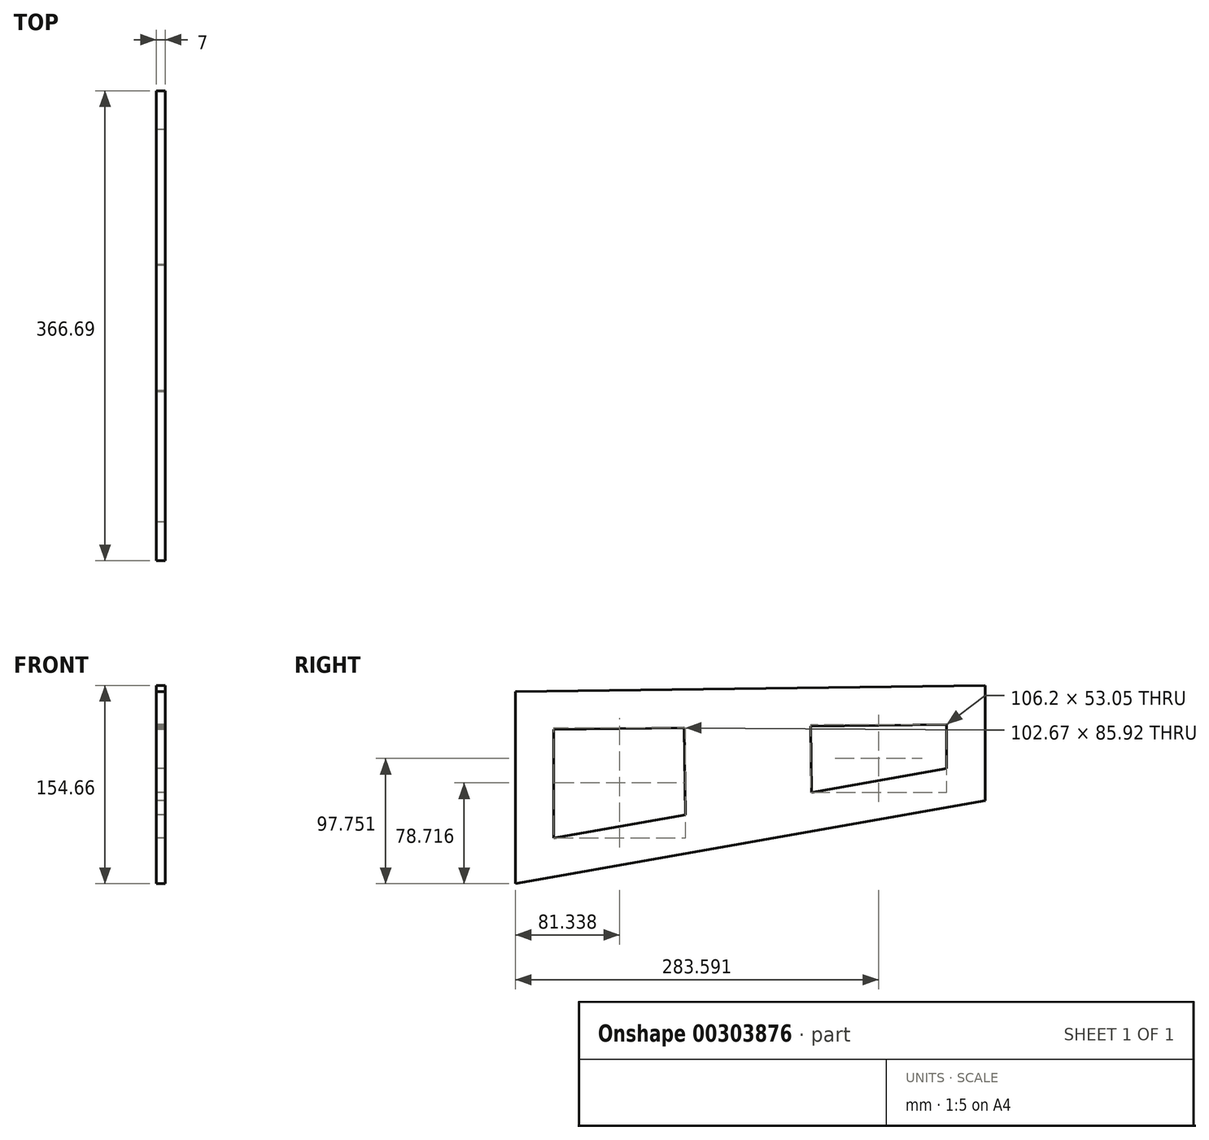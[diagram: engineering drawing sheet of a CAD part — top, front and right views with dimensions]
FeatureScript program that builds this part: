
annotation { "Feature Type Name" : "Feature", "Feature Type Description" : "" }
export const myFeature = defineFeature(function(context is Context, id is Id, definition is map)
    precondition{}
    {
        {
            var Q0;
            Q0=qCreatedBy(makeId("Right.planeOp"),FACE);
            var sketch = newSketch(context, id + "F0", { "sketchPlane" : qUnion([Q0])});
            skLineSegment(sketch, "E0.left", {"start": v(232.42, 105.9) * mm, "end": v(232.42, -44.1) * mm});
            skLineSegment(sketch, "E1.bottom", {"start": v(232.42, 105.9) * mm, "end": v(599.1, 110.55) * mm});
            skLineSegment(sketch, "E1.top", {"start": v(232.42, -44.1) * mm, "end": v(599.1, 20.55) * mm});
            skLineSegment(sketch, "E1.right", {"start": v(599.1, 110.55) * mm, "end": v(599.1, 20.55) * mm});
            skLineSegment(sketch, "E2.0", {"start": v(262.42, 76.27) * mm, "end": v(262.42, -8.35) * mm});
            skLineSegment(sketch, "E2.1", {"start": v(262.42, 76.27) * mm, "end": v(364.23, 77.57) * mm});
            skLineSegment(sketch, "E2.2", {"start": v(569.1, 80.17) * mm, "end": v(569.1, 45.72) * mm});
            skLineSegment(sketch, "E2.3", {"start": v(262.42, -8.35) * mm, "end": v(365.1, 9.75) * mm});
            skLineSegment(sketch, "E3", {"start": v(364.23, 77.57) * mm, "end": v(365.1, 9.75) * mm});
            skLineSegment(sketch, "E4", {"start": v(462.91, 78.82) * mm, "end": v(463.57, 27.11) * mm});
            skLineSegment(sketch, "E5.trimOffspring", {"start": v(462.91, 78.82) * mm, "end": v(569.1, 80.17) * mm});
            skLineSegment(sketch, "E6.trimOffspring", {"start": v(463.57, 27.11) * mm, "end": v(569.1, 45.72) * mm});
            skSolve(sketch);
        }
        {
            var Q0;
            Q0=makeQuery(id+"F0.imprint","IMPRINT",FACE,{"disambiguationData":[TD([[makeQuery(id+"F0.imprint","IMPRINT",EDGE,{"derivedFrom":sQuery(id+"F0.wireOp",EDGE,"E1.bottom")}),-1.0]])]});
            extrude(context, id + "F1", {"entities" : qUnion([Q0]), "depth" : 7 * mm});
        }
    });
